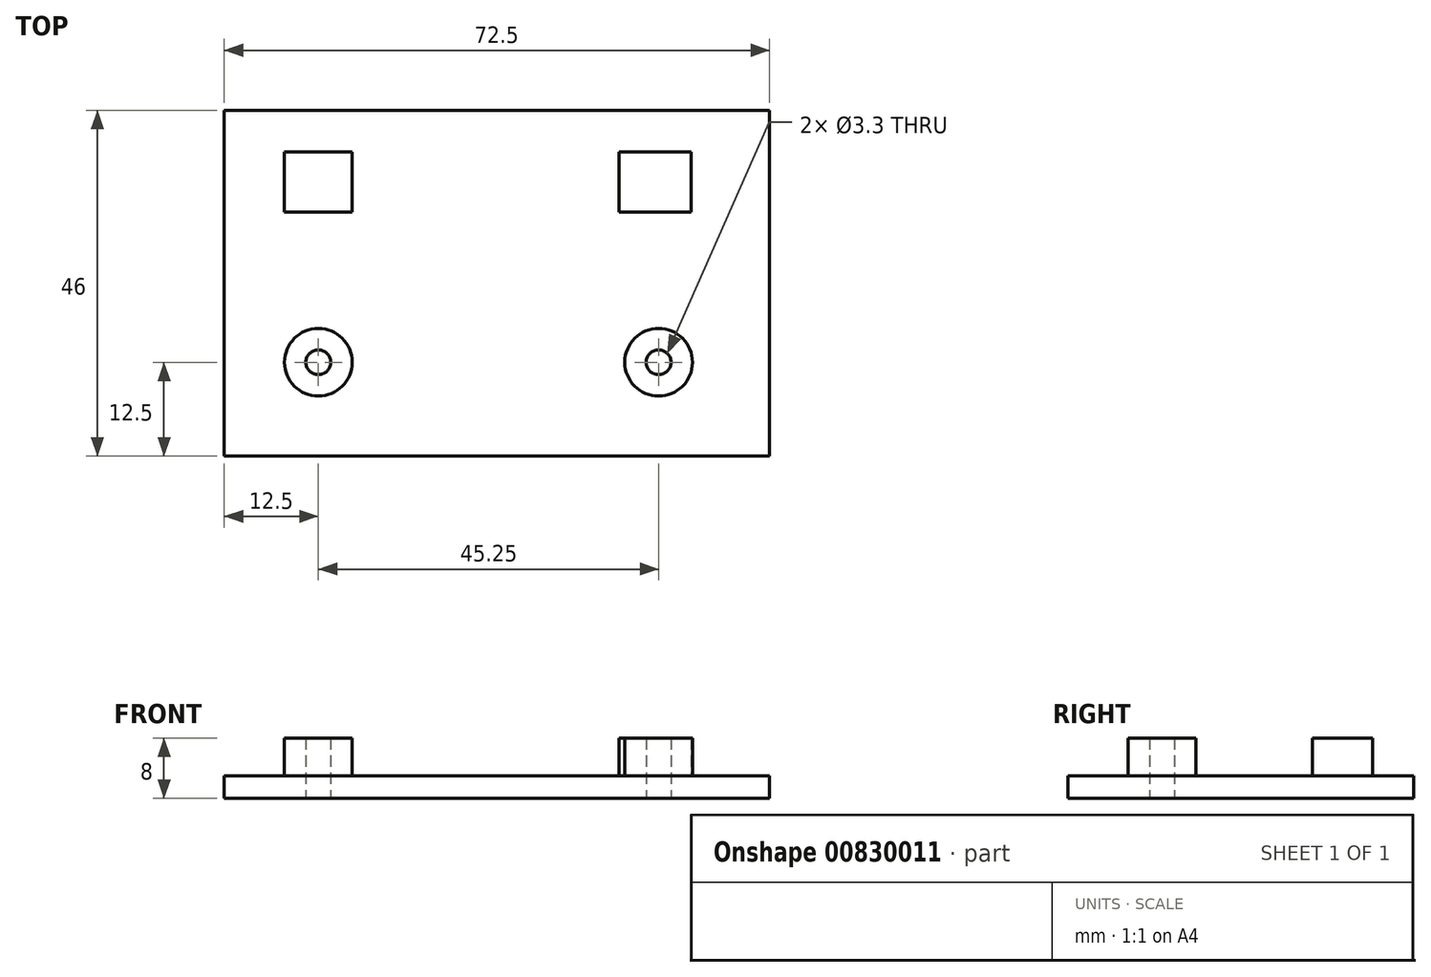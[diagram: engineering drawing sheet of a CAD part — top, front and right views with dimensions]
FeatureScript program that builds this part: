
annotation { "Feature Type Name" : "Feature", "Feature Type Description" : "" }
export const myFeature = defineFeature(function(context is Context, id is Id, definition is map)
    precondition{}
    {
        {
            var Q0;
            Q0=qCreatedBy(makeId("Top.planeOp"),FACE);
            var sketch = newSketch(context, id + "F0", { "sketchPlane" : qUnion([Q0])});
            skLineSegment(sketch, "E0.bottom", {"start": v(36.25, 23) * mm, "end": v(-36.25, 23) * mm});
            skLineSegment(sketch, "E0.top", {"start": v(36.25, -23) * mm, "end": v(-36.25, -23) * mm});
            skLineSegment(sketch, "E0.left", {"start": v(36.25, 23) * mm, "end": v(36.25, -23) * mm});
            skLineSegment(sketch, "E0.right", {"start": v(-36.25, 23) * mm, "end": v(-36.25, -23) * mm});
            skPoint(sketch, "E0.middle", {"position": v(0, 0) * mm});
            skCircle(sketch, "E1", {"center": v(-23.75, -10.5) * mm, "radius": 4.5 * mm});
            skCircle(sketch, "E2", {"center": v(21.5, -10.5) * mm, "radius": 4.5 * mm});
            skSolve(sketch);
        }
        {
            var Q0;
            Q0=makeQuery(id+"F0.imprint","IMPRINT",FACE,{"disambiguationData":[TD([[makeQuery(id+"F0.imprint","IMPRINT",EDGE,{"derivedFrom":sQuery(id+"F0.wireOp",EDGE,"E0.bottom")}),1.0]])]});
            var Q1;
            Q1=makeQuery(id+"F0.imprint","IMPRINT",FACE,{"disambiguationData":[TD([[makeQuery(id+"F0.imprint","IMPRINT",EDGE,{"derivedFrom":sQuery(id+"F0.wireOp",EDGE,"E1")}),1.0]])]});
            var Q2;
            Q2=makeQuery(id+"F0.imprint","IMPRINT",FACE,{"disambiguationData":[TD([[makeQuery(id+"F0.imprint","IMPRINT",EDGE,{"derivedFrom":sQuery(id+"F0.wireOp",EDGE,"E2")}),1.0]])]});
            extrude(context, id + "F1", {"entities" : qUnion([Q0, Q1, Q2]), "depth" : 3 * mm, "offsetDistance" : 25 * mm});
        }
        {
            var Q0;
            Q0=makeQuery(id+"F0.imprint","IMPRINT",FACE,{"disambiguationData":[TD([[makeQuery(id+"F0.imprint","IMPRINT",EDGE,{"derivedFrom":sQuery(id+"F0.wireOp",EDGE,"E1")}),1.0]])]});
            var Q1;
            Q1=makeQuery(id+"F0.imprint","IMPRINT",FACE,{"disambiguationData":[TD([[makeQuery(id+"F0.imprint","IMPRINT",EDGE,{"derivedFrom":sQuery(id+"F0.wireOp",EDGE,"E2")}),1.0]])]});
            extrude(context, id + "F2", {"entities" : qUnion([Q0, Q1]), "operationType" : NewBodyOperationType.ADD, "depth" : 8 * mm, "offsetDistance" : 25 * mm});
        }
        {
            var Q0;
            Q0=sQuery(id+"F0.wireOp",VERTEX,"E2.center");
            var Q1;
            Q1=sQuery(id+"F0.wireOp",VERTEX,"E1.center");
            var Q2;
            Q2=makeQuery(id+"F1.opExtrude","SWEPT_BODY",BODY,{"disambiguationData":[OSD([sQuery(id+"F0.wireOp",EDGE,"E0.bottom"),sQuery(id+"F0.wireOp",EDGE,"E0.top"),sQuery(id+"F0.wireOp",EDGE,"E0.left"),sQuery(id+"F0.wireOp",EDGE,"E0.right")])]});
            hole(context, id + "F3", {"style" : HoleStyle.SIMPLE, "endStyle" : HoleEndStyle.THROUGH, "oppositeDirection" : true, "standardTappedOrClearance" : lookupTablePath({ "fit" : "Normal", "standard" : "ISO", "size" : "M3", "type" : "Clearance" }), "standardBlindInLast" : lookupTablePath({ "fit" : "Standard", "standard" : "ISO", "size" : "M3", "type" : "Clearance" }), "holeDiameter" : 3.3 * mm, "majorDiameter" : 3 * mm, "isTappedThrough" : true, "tappedDepth" : 12 * mm, "tapClearance" : 3, "locations" : qUnion([Q0, Q1]), "scope" : qUnion([Q2])});
        }
        {
            var Q0;
            Q0=makeQuery(id+"F1.opExtrude","CAP_FACE",FACE,{"disambiguationData":[OSD([sQuery(id+"F0.wireOp",EDGE,"E0.bottom"),sQuery(id+"F0.wireOp",EDGE,"E0.top"),sQuery(id+"F0.wireOp",EDGE,"E0.left"),sQuery(id+"F0.wireOp",EDGE,"E0.right")])],"isStart":false});
            var sketch = newSketch(context, id + "F4", { "sketchPlane" : qUnion([Q0])});
            skLineSegment(sketch, "E3.bottom", {"start": v(-19.25, 9.5) * mm, "end": v(-28.25, 9.5) * mm});
            skLineSegment(sketch, "E3.top", {"start": v(-19.25, 17.5) * mm, "end": v(-28.25, 17.5) * mm});
            skLineSegment(sketch, "E3.left", {"start": v(-19.25, 9.5) * mm, "end": v(-19.25, 17.5) * mm});
            skLineSegment(sketch, "E3.right", {"start": v(-28.25, 9.5) * mm, "end": v(-28.25, 17.5) * mm});
            skPoint(sketch, "E3.middle", {"position": v(-23.75, 13.5) * mm});
            skSolve(sketch);
        }
        {
            var Q0;
            Q0 = qSketchRegion(id + "F4", true);
            extrude(context, id + "F5", {"entities" : qUnion([Q0]), "operationType" : NewBodyOperationType.ADD, "depth" : 5 * mm, "offsetDistance" : 25 * mm});
        }
        {
            var Q0;
            Q0=makeQuery(id+"F1.opExtrude","CAP_FACE",FACE,{"disambiguationData":[OSD([sQuery(id+"F0.wireOp",EDGE,"E0.bottom"),sQuery(id+"F0.wireOp",EDGE,"E0.top"),sQuery(id+"F0.wireOp",EDGE,"E0.left"),sQuery(id+"F0.wireOp",EDGE,"E0.right")])],"isStart":false});
            var sketch = newSketch(context, id + "F6", { "sketchPlane" : qUnion([Q0])});
            skLineSegment(sketch, "E4.bottom", {"start": v(25.85, 9.5) * mm, "end": v(16.25, 9.5) * mm});
            skLineSegment(sketch, "E4.top", {"start": v(25.85, 17.5) * mm, "end": v(16.25, 17.5) * mm});
            skLineSegment(sketch, "E4.left", {"start": v(25.85, 9.5) * mm, "end": v(25.85, 17.5) * mm});
            skLineSegment(sketch, "E4.right", {"start": v(16.25, 9.5) * mm, "end": v(16.25, 17.5) * mm});
            skPoint(sketch, "E4.middle", {"position": v(21.05, 13.5) * mm});
            skPoint(sketch, "E4.middle.positionSnap0", {"position": v(-19.25, 13.5) * mm});
            skPoint(sketch, "E4.centerSnap0", {"position": v(-19.25, 13.5) * mm});
            skSolve(sketch);
        }
        {
            var Q0;
            Q0 = qSketchRegion(id + "F6", true);
            extrude(context, id + "F7", {"entities" : qUnion([Q0]), "operationType" : NewBodyOperationType.ADD, "depth" : 5 * mm, "offsetDistance" : 25 * mm});
        }
    });
